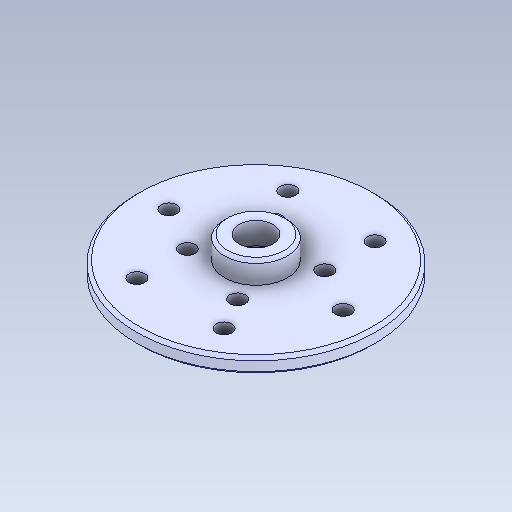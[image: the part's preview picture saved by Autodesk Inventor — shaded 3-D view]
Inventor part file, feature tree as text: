
AUTODESK INVENTOR PART (.ipt)
format: ipt  version: 2020.1 (Build 241239000, 239)  size: 157,696 bytes
history: native  units: in
note: dims shown in document units (in); Inventor stores cm internally (conversion verified against a paired STEP export)
features: chamfer x1
ambient origin geometry x8: Origin, YZ Plane, XZ Plane, XY Plane, X Axis, Y Axis, Z Axis, Center Point
bodies: Solid1 (feature_tree)
feature tree (1):
  chamfer  "Chamfer1"  [1 undecoded]
note: 1 required parameter value undecoded (feature->parameter linkage not recoverable at this tier; creation-order binding heuristic only, values carry confidence <= 0.55)
